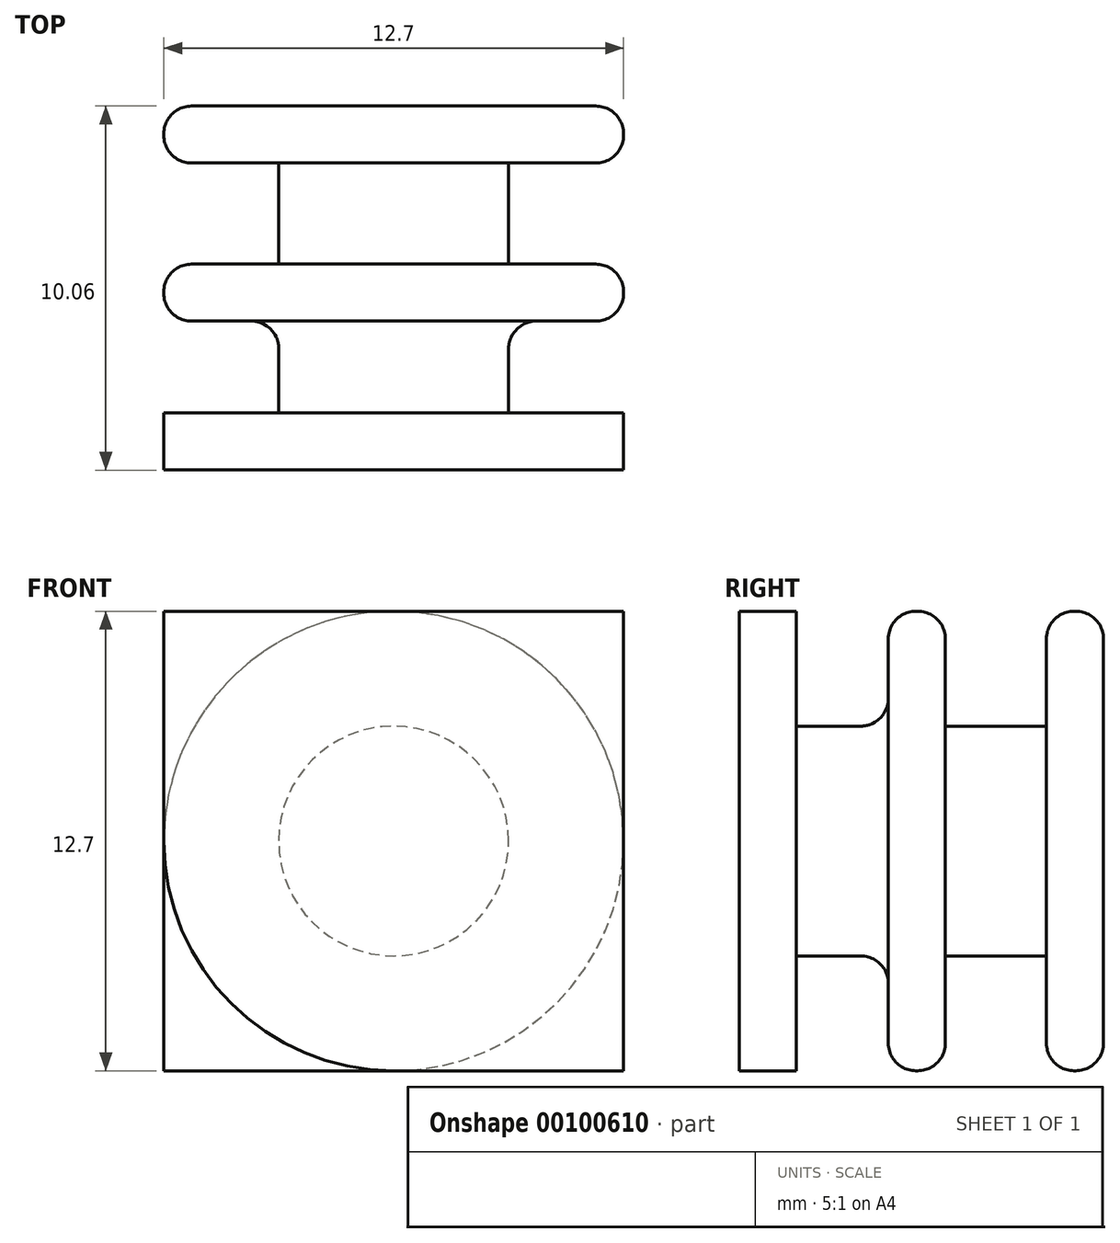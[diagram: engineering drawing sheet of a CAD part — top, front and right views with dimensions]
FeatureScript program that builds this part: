
annotation { "Feature Type Name" : "Feature", "Feature Type Description" : "" }
export const myFeature = defineFeature(function(context is Context, id is Id, definition is map)
    precondition{}
    {
        {
            var Q0;
            Q0=qCreatedBy(makeId("Front.planeOp"),FACE);
            var sketch = newSketch(context, id + "F0", { "sketchPlane" : qUnion([Q0])});
            skCircle(sketch, "E0", {"center": v(0, 0) * mm, "radius": 6.35 * mm});
            skCircle(sketch, "E1", {"center": v(0, 0) * mm, "radius": 3.18 * mm});
            skSolve(sketch);
        }
        {
            var Q0;
            Q0=makeQuery(id+"F0.imprint","IMPRINT",FACE,{"disambiguationData":[TD([[makeQuery(id+"F0.imprint","IMPRINT",EDGE,{"derivedFrom":sQuery(id+"F0.wireOp",EDGE,"E0")}),1.0]])]});
            extrude(context, id + "F1", {"entities" : qUnion([Q0]), "depth" : 1.57 * mm});
        }
        {
            var Q0;
            Q0=makeQuery(id+"F0.imprint","IMPRINT",FACE,{"disambiguationData":[TD([[makeQuery(id+"F0.imprint","IMPRINT",EDGE,{"derivedFrom":sQuery(id+"F0.wireOp",EDGE,"E1")}),1.0]])]});
            extrude(context, id + "F2", {"entities" : qUnion([Q0]), "operationType" : NewBodyOperationType.ADD, "depth" : 4.37 * mm});
        }
        {
            var Q0;
            Q0=makeQuery(id+"F2.opExtrude","CAP_FACE",FACE,{"disambiguationData":[OSD([sQuery(id+"F0.wireOp",EDGE,"E1")])],"isStart":false});
            var sketch = newSketch(context, id + "F3", { "sketchPlane" : qUnion([Q0])});
            skCircle(sketch, "E2", {"center": v(0, 0) * mm, "radius": 6.35 * mm});
            skSolve(sketch);
        }
        {
            var Q0;
            Q0=makeQuery(id+"F3.imprint","IMPRINT",FACE,{"disambiguationData":[TD([[makeQuery(id+"F3.imprint","IMPRINT",EDGE,{"derivedFrom":makeQuery(id+"F2.opExtrude","CAP_EDGE",EDGE,{"disambiguationData":[OSD([sQuery(id+"F0.wireOp",EDGE,"E1")])],"isStart":false})}),1.0]])]});
            var Q1;
            Q1=makeQuery(id+"F3.imprint","IMPRINT",FACE,{"disambiguationData":[TD([[makeQuery(id+"F3.imprint","IMPRINT",EDGE,{"derivedFrom":sQuery(id+"F3.wireOp",EDGE,"E2")}),1.0]])]});
            extrude(context, id + "F4", {"entities" : qUnion([Q0, Q1]), "operationType" : NewBodyOperationType.ADD, "depth" : 1.57 * mm});
        }
        {
            var Q0;
            Q0=makeQuery(id+"F4.opExtrude","CAP_FACE",FACE,{"disambiguationData":[OSD([sQuery(id+"F3.wireOp",EDGE,"E2")])],"isStart":false});
            var sketch = newSketch(context, id + "F5", { "sketchPlane" : qUnion([Q0])});
            skCircle(sketch, "E3", {"center": v(0, 0) * mm, "radius": 3.18 * mm});
            skSolve(sketch);
        }
        {
            var Q0;
            Q0=makeQuery(id+"F5.imprint","IMPRINT",FACE,{"disambiguationData":[TD([[makeQuery(id+"F5.imprint","IMPRINT",EDGE,{"derivedFrom":sQuery(id+"F5.wireOp",EDGE,"E3")}),1.0]])]});
            var Q1;
            Q1=sQuery(id+"F5.wireOp",EDGE,"E3");
            extrude(context, id + "F6", {"entities" : qUnion([Q0]), "operationType" : NewBodyOperationType.ADD, "surfaceEntities" : qUnion([Q1]), "depth" : 2.54 * mm});
        }
        {
            var Q0;
            Q0=makeQuery(id+"F6.opExtrude","CAP_FACE",FACE,{"disambiguationData":[OSD([sQuery(id+"F5.wireOp",EDGE,"E3")])],"isStart":false});
            var sketch = newSketch(context, id + "F7", { "sketchPlane" : qUnion([Q0])});
            skLineSegment(sketch, "E4.bottom", {"start": v(6.35, 6.35) * mm, "end": v(-6.35, 6.35) * mm});
            skLineSegment(sketch, "E4.top", {"start": v(6.35, -6.35) * mm, "end": v(-6.35, -6.35) * mm});
            skLineSegment(sketch, "E4.left", {"start": v(6.35, 6.35) * mm, "end": v(6.35, -6.35) * mm});
            skLineSegment(sketch, "E4.right", {"start": v(-6.35, 6.35) * mm, "end": v(-6.35, -6.35) * mm});
            skPoint(sketch, "E4.middle", {"position": v(0, 0) * mm});
            skSolve(sketch);
        }
        {
            var Q0;
            Q0=makeQuery(id+"F7.imprint","IMPRINT",FACE,{"disambiguationData":[TD([[makeQuery(id+"F7.imprint","IMPRINT",EDGE,{"derivedFrom":makeQuery(id+"F6.opExtrude","CAP_EDGE",EDGE,{"disambiguationData":[OSD([sQuery(id+"F5.wireOp",EDGE,"E3")])],"isStart":false})}),1.0]])]});
            var Q1;
            Q1=makeQuery(id+"F7.imprint","IMPRINT",FACE,{"disambiguationData":[TD([[makeQuery(id+"F7.imprint","IMPRINT",EDGE,{"derivedFrom":sQuery(id+"F7.wireOp",EDGE,"E4.bottom")}),1.0]])]});
            extrude(context, id + "F8", {"entities" : qUnion([Q0, Q1]), "operationType" : NewBodyOperationType.ADD, "depth" : 1.57 * mm});
        }
        {
            var Q0;
            Q0=makeQuery(id+"F4.opExtrude","CAP_EDGE",EDGE,{"disambiguationData":[OSD([sQuery(id+"F3.wireOp",EDGE,"E2")])],"isStart":false});
            var Q1;
            Q1=makeQuery(id+"F4.opExtrude","CAP_EDGE",EDGE,{"disambiguationData":[OSD([sQuery(id+"F3.wireOp",EDGE,"E2")])],"isStart":true});
            var Q2;
            Q2=makeQuery(id+"F1.opExtrude","CAP_EDGE",EDGE,{"disambiguationData":[OSD([sQuery(id+"F0.wireOp",EDGE,"E0")])],"isStart":false});
            var Q3;
            Q3=makeQuery(id+"F1.opExtrude","CAP_EDGE",EDGE,{"disambiguationData":[OSD([sQuery(id+"F0.wireOp",EDGE,"E0")])],"isStart":true});
            var Q4;
            Q4=makeQuery(id+"F1.opExtrude","CAP_EDGE",EDGE,{"disambiguationData":[OSD([sQuery(id+"F0.wireOp",EDGE,"E1")])],"isStart":false});
            var Q5;
            Q5=makeQuery(id+"F2.opExtrude","CAP_EDGE",EDGE,{"disambiguationData":[OSD([sQuery(id+"F0.wireOp",EDGE,"E1")])],"isStart":false});
            var Q6;
            Q6=makeQuery(id+"F4.opExtrude","CAP_FACE",FACE,{"disambiguationData":[OSD([sQuery(id+"F3.wireOp",EDGE,"E2")])],"isStart":false});
            var Q7;
            Q7=makeQuery(id+"F6.opExtrude","CAP_EDGE",EDGE,{"disambiguationData":[OSD([sQuery(id+"F5.wireOp",EDGE,"E3")])],"isStart":false});
            fillet(context, id + "F9", {"entities" : qUnion([Q0, Q1, Q2, Q3, Q4, Q5, Q6, Q7]), "radius" : 0.76 * mm, "tangentPropagation" : true, "allowEdgeOverflow" : false});
        }
    });
